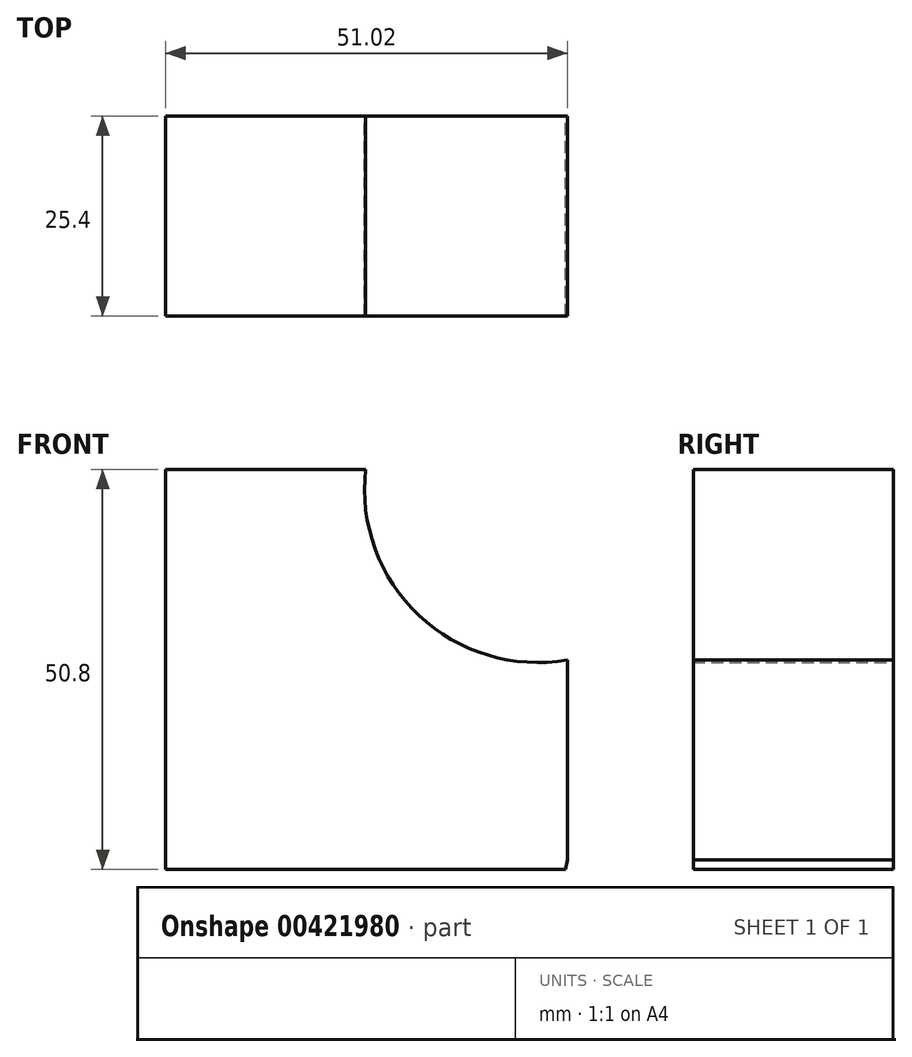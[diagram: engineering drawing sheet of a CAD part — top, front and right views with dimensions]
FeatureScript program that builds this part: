
annotation { "Feature Type Name" : "Feature", "Feature Type Description" : "" }
export const myFeature = defineFeature(function(context is Context, id is Id, definition is map)
    precondition{}
    {
        {
            var Q0;
            Q0=qCreatedBy(makeId("Front.planeOp"),FACE);
            var sketch = newSketch(context, id + "F0", { "sketchPlane" : qUnion([Q0])});
            skLineSegment(sketch, "E0", {"start": v(0, 0) * mm, "end": v(-50.8, 0) * mm});
            skLineSegment(sketch, "E1", {"start": v(-50.8, 0) * mm, "end": v(-50.8, 50.8) * mm});
            skLineSegment(sketch, "E2", {"start": v(-50.8, 50.8) * mm, "end": v(-25.4, 50.8) * mm});
            skLineSegment(sketch, "E3", {"start": v(0.22, 1.2) * mm, "end": v(0.22, 26.6) * mm});
            skArc(sketch, "E4", {"start": v(-25.4, 50.8) * mm, "mid": v(-18.64, 32.3) * mm, "end": v(0.22, 26.6) * mm});
            skLineSegment(sketch, "E5", {"start": v(0, 0) * mm, "end": v(0.22, 1.2) * mm});
            skSolve(sketch);
        }
        {
            var Q0;
            Q0=makeQuery(id+"F0.imprint","IMPRINT",FACE,{"disambiguationData":[TD([[makeQuery(id+"F0.imprint","IMPRINT",EDGE,{"derivedFrom":sQuery(id+"F0.wireOp",EDGE,"E0")}),-1.0]])]});
            extrude(context, id + "F1", {"entities" : qUnion([Q0]), "depth" : 25.4 * mm});
        }
    });
